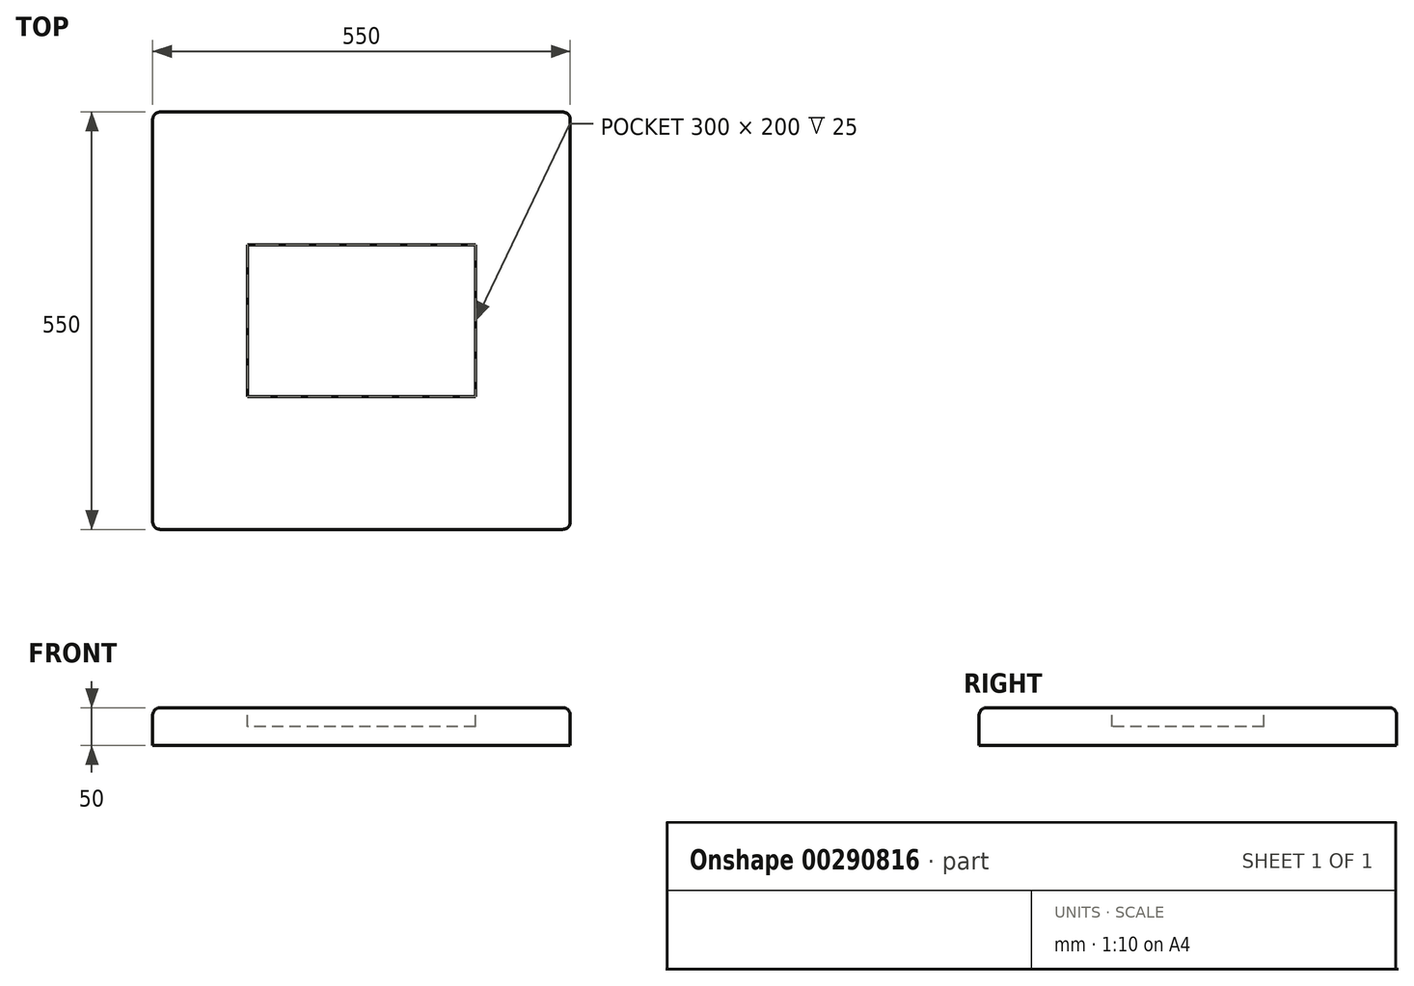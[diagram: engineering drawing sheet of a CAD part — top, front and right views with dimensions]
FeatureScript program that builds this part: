
annotation { "Feature Type Name" : "Feature", "Feature Type Description" : "" }
export const myFeature = defineFeature(function(context is Context, id is Id, definition is map)
    precondition{}
    {
        {
            var Q0;
            Q0=qCreatedBy(makeId("Top.planeOp"),FACE);
            var sketch = newSketch(context, id + "F0", { "sketchPlane" : qUnion([Q0])});
            skLineSegment(sketch, "E0.bottom", {"start": v(275, 275) * mm, "end": v(-275, 275) * mm});
            skLineSegment(sketch, "E0.top", {"start": v(275, -275) * mm, "end": v(-275, -275) * mm});
            skLineSegment(sketch, "E0.left", {"start": v(275, 275) * mm, "end": v(275, -275) * mm});
            skLineSegment(sketch, "E0.right", {"start": v(-275, 275) * mm, "end": v(-275, -275) * mm});
            skPoint(sketch, "E0.middle", {"position": v(0, 0) * mm});
            skSolve(sketch);
        }
        {
            var Q0;
            Q0=makeQuery(id+"F0.imprint","IMPRINT",FACE,{"disambiguationData":[TD([[makeQuery(id+"F0.imprint","IMPRINT",EDGE,{"derivedFrom":sQuery(id+"F0.wireOp",EDGE,"E0.bottom")}),1.0]])]});
            extrude(context, id + "F1", {"entities" : qUnion([Q0]), "depth" : 50 * mm});
        }
        {
            var Q0;
            Q0=makeQuery(id+"F1.opExtrude","CAP_EDGE",EDGE,{"disambiguationData":[OSD([sQuery(id+"F0.wireOp",EDGE,"E0.top")])],"isStart":false});
            var Q1;
            Q1=makeQuery(id+"F1.opExtrude","CAP_EDGE",EDGE,{"disambiguationData":[OSD([sQuery(id+"F0.wireOp",EDGE,"E0.left")])],"isStart":false});
            var Q2;
            Q2=makeQuery(id+"F1.opExtrude","CAP_EDGE",EDGE,{"disambiguationData":[OSD([sQuery(id+"F0.wireOp",EDGE,"E0.bottom")])],"isStart":false});
            var Q3;
            Q3=makeQuery(id+"F1.opExtrude","CAP_EDGE",EDGE,{"disambiguationData":[OSD([sQuery(id+"F0.wireOp",EDGE,"E0.right")])],"isStart":false});
            fillet(context, id + "F2", {"entities" : qUnion([Q0, Q1, Q2, Q3]), "radius" : 10 * mm, "tangentPropagation" : true, "allowEdgeOverflow" : false});
        }
        {
            var Q0;
            Q0=makeQuery(id+"F1.opExtrude","SWEPT_EDGE",EDGE,{"disambiguationData":[OSD([sQuery(id+"F0.wireOp",EDGE,"E0.top"),sQuery(id+"F0.wireOp",EDGE,"E0.left")])]});
            var Q1;
            Q1=makeQuery(id+"F1.opExtrude","SWEPT_EDGE",EDGE,{"disambiguationData":[OSD([sQuery(id+"F0.wireOp",EDGE,"E0.top"),sQuery(id+"F0.wireOp",EDGE,"E0.right")])]});
            var Q2;
            Q2=makeQuery(id+"F1.opExtrude","SWEPT_EDGE",EDGE,{"disambiguationData":[OSD([sQuery(id+"F0.wireOp",EDGE,"E0.bottom"),sQuery(id+"F0.wireOp",EDGE,"E0.right")])]});
            var Q3;
            Q3=makeQuery(id+"F1.opExtrude","SWEPT_EDGE",EDGE,{"disambiguationData":[OSD([sQuery(id+"F0.wireOp",EDGE,"E0.bottom"),sQuery(id+"F0.wireOp",EDGE,"E0.left")])]});
            fillet(context, id + "F3", {"entities" : qUnion([Q0, Q1, Q2, Q3]), "radius" : 10 * mm, "tangentPropagation" : true, "allowEdgeOverflow" : false});
        }
        {
            var Q0;
            Q0=makeQuery(id+"F1.opExtrude","CAP_FACE",FACE,{"disambiguationData":[OSD([sQuery(id+"F0.wireOp",EDGE,"E0.bottom"),sQuery(id+"F0.wireOp",EDGE,"E0.top"),sQuery(id+"F0.wireOp",EDGE,"E0.left"),sQuery(id+"F0.wireOp",EDGE,"E0.right")])],"isStart":false});
            var sketch = newSketch(context, id + "F4", { "sketchPlane" : qUnion([Q0])});
            skLineSegment(sketch, "E1.bottom", {"start": v(150, 100) * mm, "end": v(-150, 100) * mm});
            skLineSegment(sketch, "E1.top", {"start": v(150, -100) * mm, "end": v(-150, -100) * mm});
            skLineSegment(sketch, "E1.left", {"start": v(150, 100) * mm, "end": v(150, -100) * mm});
            skLineSegment(sketch, "E1.right", {"start": v(-150, 100) * mm, "end": v(-150, -100) * mm});
            skPoint(sketch, "E1.middle", {"position": v(0, 0) * mm});
            skSolve(sketch);
        }
        {
            var Q0;
            Q0=makeQuery(id+"F4.imprint","IMPRINT",FACE,{"disambiguationData":[TD([[makeQuery(id+"F4.imprint","IMPRINT",EDGE,{"derivedFrom":sQuery(id+"F4.wireOp",EDGE,"E1.bottom")}),1.0]])]});
            extrude(context, id + "F5", {"entities" : qUnion([Q0]), "operationType" : NewBodyOperationType.REMOVE, "oppositeDirection" : true, "depth" : 25 * mm});
        }
    });
